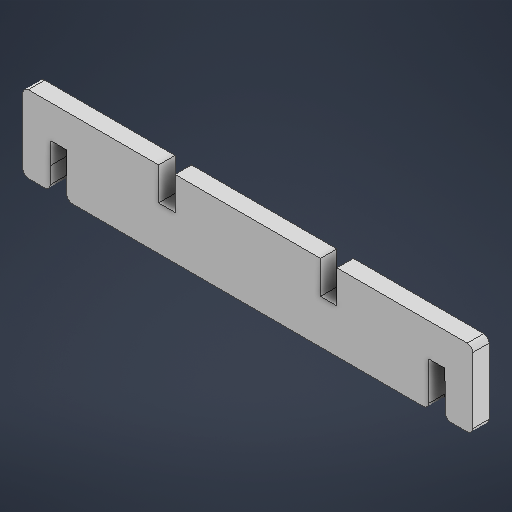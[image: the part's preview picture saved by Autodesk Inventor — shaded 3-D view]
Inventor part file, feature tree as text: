
AUTODESK INVENTOR PART (.ipt)
format: ipt  version: 2025.3 (Build 293356030, 356C)  size: 227,328 bytes
history: native  units: mm
features: other x1, extrude x1, sketch x1
ambient origin geometry x8: Origin, YZ Plane, XZ Plane, XY Plane, X Axis, Y Axis, Z Axis, Center Point
bodies: Body1 (feature_tree)
feature tree (3):
  other  "實體1"
  extrude  "擠出1"  Depth=10.0mm
  sketch  "草圖1"
